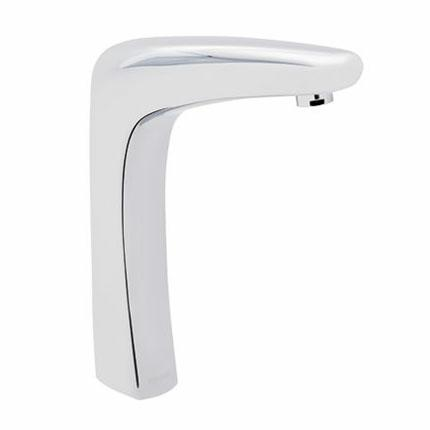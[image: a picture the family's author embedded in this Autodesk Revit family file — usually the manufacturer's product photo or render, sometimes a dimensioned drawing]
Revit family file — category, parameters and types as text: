
# Revit family: Llave Electronica TV302-1.5
name_source: partatom
category: Aparatos sanitarios
revit_build: Autodesk Revit 2016 (Build: 20150220_1215(x64)
units: mm (PartAtom-declared; Revit-internal decimal feet)

## family parameters
Compartido = Sí
Corte con vacíos al cargar = No
Cota de conector redondo = Diámetro de uso
Número OmniClass = 23.45.00.00
Punto de cálculo de habitación = Sí
Se basa en plano de trabajo = Sí
Siempre vertical = Sí
Tipo de pieza = Normal
Título OmniClass = Sanitary, Laundry, and Cleaning Equipment

## types (1)
- TV302-1.5
    Chrome = Brass Chromed
    Comentarios de tipo = Electronic Line
    Conexión AF = Sí
    Connection = ½" - 14 NPSM
    Descripción = Electronic Faucet Lavatory Current Argos
    Detection Range = 1.9" (50 mm) - 8.7" (220 mm)
    Elevación por Defecto = 1"
    Elevación por defecto = 48"
    Fabricante = Helvex
    Features = Infrared Sensor, Filter with Check Valve Maintenance
    Feeding Voltage = 127 V
    Imagen de tipo = TV302-1.5.jpg
    Max. Working Pressure = 85.3 psi
    Min. Working Pressure = 10.0 psi
    Modelo = TV302-1.5
    Power Consumption = 3 W
    Total Height = 11"
    Total Width = 9"
    URL = https://www.helvex.com.mx

## geometry (parser evidence)
native form markers: Sweep x3
no freeform markers — native parametric forms only
